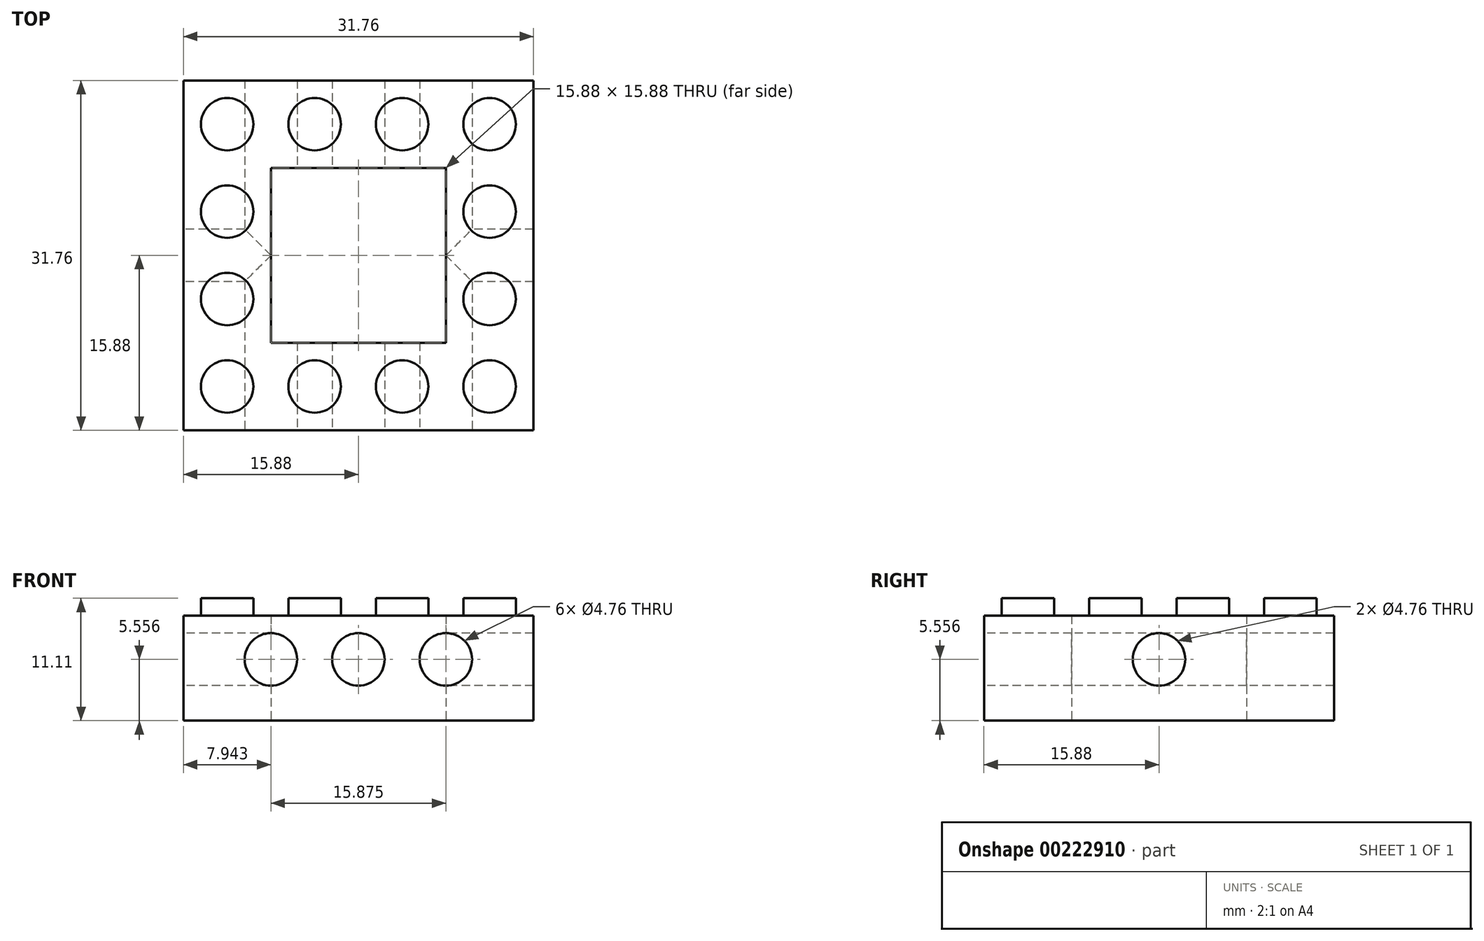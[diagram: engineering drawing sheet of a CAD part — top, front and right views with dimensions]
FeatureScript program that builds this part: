
annotation { "Feature Type Name" : "Feature", "Feature Type Description" : "" }
export const myFeature = defineFeature(function(context is Context, id is Id, definition is map)
    precondition{}
    {
        {
            var Q0;
            Q0=qCreatedBy(makeId("Top.planeOp"),FACE);
            var sketch = newSketch(context, id + "F0", { "sketchPlane" : qUnion([Q0])});
            skLineSegment(sketch, "E0.bottom", {"start": v(-15.88, 15.88) * mm, "end": v(15.88, 15.88) * mm});
            skLineSegment(sketch, "E0.top", {"start": v(-15.88, -15.88) * mm, "end": v(15.88, -15.88) * mm});
            skLineSegment(sketch, "E0.left", {"start": v(-15.87, 15.88) * mm, "end": v(-15.88, -15.88) * mm});
            skLineSegment(sketch, "E0.right", {"start": v(15.88, 15.88) * mm, "end": v(15.88, -15.88) * mm});
            skPoint(sketch, "E0.middle", {"position": v(0, 0) * mm});
            skCircle(sketch, "E1", {"center": v(-11.9, -11.9) * mm, "radius": 2.38 * mm});
            skCircle(sketch, "E2.0.1.0", {"center": v(-11.9, -3.97) * mm, "radius": 2.38 * mm});
            skCircle(sketch, "E2.0.2.0", {"center": v(-11.9, 3.97) * mm, "radius": 2.38 * mm});
            skCircle(sketch, "E2.0.3.0", {"center": v(-11.9, 11.9) * mm, "radius": 2.38 * mm});
            skCircle(sketch, "E2.1.0.0", {"center": v(-3.97, -11.9) * mm, "radius": 2.38 * mm});
            skCircle(sketch, "E2.1.1.0", {"center": v(-3.97, -3.97) * mm, "radius": 2.38 * mm});
            skCircle(sketch, "E2.1.2.0", {"center": v(-3.97, 3.97) * mm, "radius": 2.38 * mm});
            skCircle(sketch, "E2.1.3.0", {"center": v(-3.97, 11.9) * mm, "radius": 2.38 * mm});
            skCircle(sketch, "E2.2.0.0", {"center": v(3.97, -11.9) * mm, "radius": 2.38 * mm});
            skCircle(sketch, "E2.2.1.0", {"center": v(3.97, -3.97) * mm, "radius": 2.38 * mm});
            skCircle(sketch, "E2.2.2.0", {"center": v(3.97, 3.97) * mm, "radius": 2.38 * mm});
            skCircle(sketch, "E2.2.3.0", {"center": v(3.97, 11.9) * mm, "radius": 2.38 * mm});
            skCircle(sketch, "E2.3.0.0", {"center": v(11.9, -11.9) * mm, "radius": 2.38 * mm});
            skCircle(sketch, "E2.3.1.0", {"center": v(11.9, -3.97) * mm, "radius": 2.38 * mm});
            skCircle(sketch, "E2.3.2.0", {"center": v(11.9, 3.97) * mm, "radius": 2.38 * mm});
            skCircle(sketch, "E2.3.3.0", {"center": v(11.9, 11.9) * mm, "radius": 2.38 * mm});
            skLineSegment(sketch, "E2.direction1", {"start": v(-11.9, -11.9) * mm, "end": v(-3.97, -11.9) * mm, "construction": true});
            skLineSegment(sketch, "E2.direction2", {"start": v(-11.9, -11.9) * mm, "end": v(-11.9, -3.97) * mm, "construction": true});
            skSolve(sketch);
        }
        {
            var Q0;
            Q0 = qSketchRegion(id + "F0", true);
            extrude(context, id + "F1", {"entities" : qUnion([Q0]), "depth" : 9.52 * mm});
        }
        {
            var Q0;
            Q0=makeQuery(id+"F0.imprint","IMPRINT",FACE,{"disambiguationData":[TD([[makeQuery(id+"F0.imprint","IMPRINT",EDGE,{"derivedFrom":sQuery(id+"F0.wireOp",EDGE,"E2.0.3.0")}),1.0]])]});
            var Q1;
            Q1=makeQuery(id+"F0.imprint","IMPRINT",FACE,{"disambiguationData":[TD([[makeQuery(id+"F0.imprint","IMPRINT",EDGE,{"derivedFrom":sQuery(id+"F0.wireOp",EDGE,"E2.1.3.0")}),1.0]])]});
            var Q2;
            Q2=makeQuery(id+"F0.imprint","IMPRINT",FACE,{"disambiguationData":[TD([[makeQuery(id+"F0.imprint","IMPRINT",EDGE,{"derivedFrom":sQuery(id+"F0.wireOp",EDGE,"E2.2.3.0")}),1.0]])]});
            var Q3;
            Q3=makeQuery(id+"F0.imprint","IMPRINT",FACE,{"disambiguationData":[TD([[makeQuery(id+"F0.imprint","IMPRINT",EDGE,{"derivedFrom":sQuery(id+"F0.wireOp",EDGE,"E2.3.3.0")}),1.0]])]});
            var Q4;
            Q4=makeQuery(id+"F0.imprint","IMPRINT",FACE,{"disambiguationData":[TD([[makeQuery(id+"F0.imprint","IMPRINT",EDGE,{"derivedFrom":sQuery(id+"F0.wireOp",EDGE,"E2.3.2.0")}),1.0]])]});
            var Q5;
            Q5=makeQuery(id+"F0.imprint","IMPRINT",FACE,{"disambiguationData":[TD([[makeQuery(id+"F0.imprint","IMPRINT",EDGE,{"derivedFrom":sQuery(id+"F0.wireOp",EDGE,"E2.2.2.0")}),1.0]])]});
            var Q6;
            Q6=makeQuery(id+"F0.imprint","IMPRINT",FACE,{"disambiguationData":[TD([[makeQuery(id+"F0.imprint","IMPRINT",EDGE,{"derivedFrom":sQuery(id+"F0.wireOp",EDGE,"E2.1.2.0")}),1.0]])]});
            var Q7;
            Q7=makeQuery(id+"F0.imprint","IMPRINT",FACE,{"disambiguationData":[TD([[makeQuery(id+"F0.imprint","IMPRINT",EDGE,{"derivedFrom":sQuery(id+"F0.wireOp",EDGE,"E2.0.2.0")}),1.0]])]});
            var Q8;
            Q8=makeQuery(id+"F0.imprint","IMPRINT",FACE,{"disambiguationData":[TD([[makeQuery(id+"F0.imprint","IMPRINT",EDGE,{"derivedFrom":sQuery(id+"F0.wireOp",EDGE,"E2.0.1.0")}),1.0]])]});
            var Q9;
            Q9=makeQuery(id+"F0.imprint","IMPRINT",FACE,{"disambiguationData":[TD([[makeQuery(id+"F0.imprint","IMPRINT",EDGE,{"derivedFrom":sQuery(id+"F0.wireOp",EDGE,"E2.1.1.0")}),1.0]])]});
            var Q10;
            Q10=makeQuery(id+"F0.imprint","IMPRINT",FACE,{"disambiguationData":[TD([[makeQuery(id+"F0.imprint","IMPRINT",EDGE,{"derivedFrom":sQuery(id+"F0.wireOp",EDGE,"E2.2.1.0")}),1.0]])]});
            var Q11;
            Q11=makeQuery(id+"F0.imprint","IMPRINT",FACE,{"disambiguationData":[TD([[makeQuery(id+"F0.imprint","IMPRINT",EDGE,{"derivedFrom":sQuery(id+"F0.wireOp",EDGE,"E2.3.1.0")}),1.0]])]});
            var Q12;
            Q12=makeQuery(id+"F0.imprint","IMPRINT",FACE,{"disambiguationData":[TD([[makeQuery(id+"F0.imprint","IMPRINT",EDGE,{"derivedFrom":sQuery(id+"F0.wireOp",EDGE,"E2.3.0.0")}),1.0]])]});
            var Q13;
            Q13=makeQuery(id+"F0.imprint","IMPRINT",FACE,{"disambiguationData":[TD([[makeQuery(id+"F0.imprint","IMPRINT",EDGE,{"derivedFrom":sQuery(id+"F0.wireOp",EDGE,"E2.2.0.0")}),1.0]])]});
            var Q14;
            Q14=makeQuery(id+"F0.imprint","IMPRINT",FACE,{"disambiguationData":[TD([[makeQuery(id+"F0.imprint","IMPRINT",EDGE,{"derivedFrom":sQuery(id+"F0.wireOp",EDGE,"E2.1.0.0")}),1.0]])]});
            var Q15;
            Q15=makeQuery(id+"F0.imprint","IMPRINT",FACE,{"disambiguationData":[TD([[makeQuery(id+"F0.imprint","IMPRINT",EDGE,{"derivedFrom":sQuery(id+"F0.wireOp",EDGE,"E1")}),1.0]])]});
            extrude(context, id + "F2", {"entities" : qUnion([Q0, Q1, Q2, Q3, Q4, Q5, Q6, Q7, Q8, Q9, Q10, Q11, Q12, Q13, Q14, Q15]), "operationType" : NewBodyOperationType.ADD, "depth" : 11.1 * mm});
        }
        {
            var Q0;
            Q0=makeQuery(id+"F1.opExtrude","CAP_FACE",FACE,{"disambiguationData":[OSD([sQuery(id+"F0.wireOp",EDGE,"E0.bottom"),sQuery(id+"F0.wireOp",EDGE,"E0.top"),sQuery(id+"F0.wireOp",EDGE,"E0.left"),sQuery(id+"F0.wireOp",EDGE,"E0.right"),sQuery(id+"F0.wireOp",EDGE,"E1"),sQuery(id+"F0.wireOp",EDGE,"E2.0.1.0"),sQuery(id+"F0.wireOp",EDGE,"E2.0.2.0"),sQuery(id+"F0.wireOp",EDGE,"E2.0.3.0"),sQuery(id+"F0.wireOp",EDGE,"E2.1.0.0"),sQuery(id+"F0.wireOp",EDGE,"E2.1.1.0"),sQuery(id+"F0.wireOp",EDGE,"E2.1.2.0"),sQuery(id+"F0.wireOp",EDGE,"E2.1.3.0"),sQuery(id+"F0.wireOp",EDGE,"E2.2.0.0"),sQuery(id+"F0.wireOp",EDGE,"E2.2.1.0"),sQuery(id+"F0.wireOp",EDGE,"E2.2.2.0"),sQuery(id+"F0.wireOp",EDGE,"E2.2.3.0"),sQuery(id+"F0.wireOp",EDGE,"E2.3.0.0"),sQuery(id+"F0.wireOp",EDGE,"E2.3.1.0"),sQuery(id+"F0.wireOp",EDGE,"E2.3.2.0"),sQuery(id+"F0.wireOp",EDGE,"E2.3.3.0")])],"isStart":false});
            var sketch = newSketch(context, id + "F3", { "sketchPlane" : qUnion([Q0])});
            skLineSegment(sketch, "E3.bottom", {"start": v(-7.94, 7.94) * mm, "end": v(7.94, 7.94) * mm});
            skLineSegment(sketch, "E3.top", {"start": v(-7.94, -7.94) * mm, "end": v(7.94, -7.94) * mm});
            skLineSegment(sketch, "E3.left", {"start": v(-7.94, 7.94) * mm, "end": v(-7.94, -7.94) * mm});
            skLineSegment(sketch, "E3.right", {"start": v(7.94, 7.94) * mm, "end": v(7.94, -7.94) * mm});
            skPoint(sketch, "E3.middle", {"position": v(0, 0) * mm});
            skSolve(sketch);
        }
        {
            var Q0;
            Q0 = qSketchRegion(id + "F3", true);
            extrude(context, id + "F4", {"entities" : qUnion([Q0]), "operationType" : NewBodyOperationType.REMOVE, "endBound" : BoundingType.SYMMETRIC, "depth" : 25.4 * mm});
        }
        {
            var Q0;
            Q0=makeQuery(id+"F1.opExtrude","SWEPT_FACE",FACE,{"disambiguationData":[OSD([sQuery(id+"F0.wireOp",EDGE,"E0.top")])]});
            var sketch = newSketch(context, id + "F5", { "sketchPlane" : qUnion([Q0])});
            skCircle(sketch, "E4", {"center": v(0, 5.56) * mm, "radius": 2.38 * mm});
            skCircle(sketch, "E5", {"center": v(-7.94, 5.56) * mm, "radius": 2.38 * mm});
            skCircle(sketch, "E6", {"center": v(7.94, 5.56) * mm, "radius": 2.38 * mm});
            skSolve(sketch);
        }
        {
            var Q0;
            Q0=makeQuery(id+"F5.imprint","IMPRINT",FACE,{"disambiguationData":[TD([[makeQuery(id+"F5.imprint","IMPRINT",EDGE,{"derivedFrom":sQuery(id+"F5.wireOp",EDGE,"E6")}),1.0]])]});
            var Q1;
            Q1=makeQuery(id+"F5.imprint","IMPRINT",FACE,{"disambiguationData":[TD([[makeQuery(id+"F5.imprint","IMPRINT",EDGE,{"derivedFrom":sQuery(id+"F5.wireOp",EDGE,"E4")}),1.0]])]});
            var Q2;
            Q2=makeQuery(id+"F5.imprint","IMPRINT",FACE,{"disambiguationData":[TD([[makeQuery(id+"F5.imprint","IMPRINT",EDGE,{"derivedFrom":sQuery(id+"F5.wireOp",EDGE,"E5")}),1.0]])]});
            extrude(context, id + "F6", {"entities" : qUnion([Q0, Q1, Q2]), "operationType" : NewBodyOperationType.REMOVE, "oppositeDirection" : true, "depth" : 50.8 * mm});
        }
        {
            var Q0;
            Q0=makeQuery(id+"F1.opExtrude","SWEPT_FACE",FACE,{"disambiguationData":[OSD([sQuery(id+"F0.wireOp",EDGE,"E0.left")])]});
            var sketch = newSketch(context, id + "F7", { "sketchPlane" : qUnion([Q0])});
            skLineSegment(sketch, "E7", {"start": v(0, 0) * mm, "end": v(0, 5.56) * mm});
            skCircle(sketch, "E8", {"center": v(0, 5.56) * mm, "radius": 2.38 * mm});
            skSolve(sketch);
        }
        {
            var Q0;
            Q0 = qSketchRegion(id + "F7", true);
            extrude(context, id + "F8", {"entities" : qUnion([Q0]), "operationType" : NewBodyOperationType.REMOVE, "oppositeDirection" : true, "depth" : 50.8 * mm});
        }
    });
